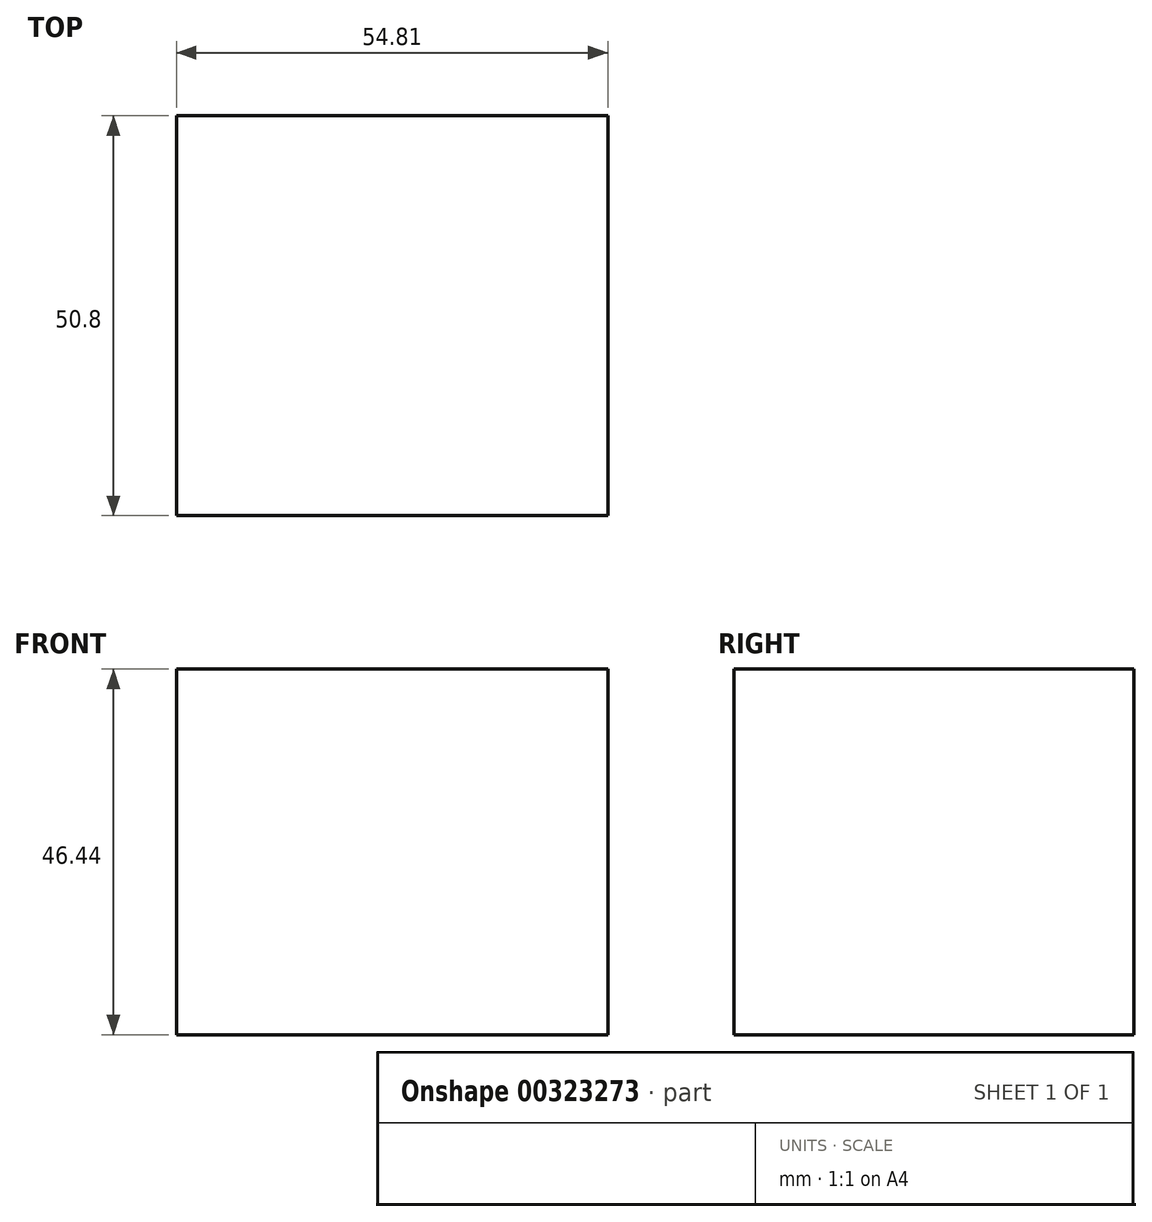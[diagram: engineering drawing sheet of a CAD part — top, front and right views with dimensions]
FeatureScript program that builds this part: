
annotation { "Feature Type Name" : "Feature", "Feature Type Description" : "" }
export const myFeature = defineFeature(function(context is Context, id is Id, definition is map)
    precondition{}
    {
        {
            var Q0;
            Q0=qCreatedBy(makeId("Front.planeOp"),FACE);
            var sketch = newSketch(context, id + "F0", { "sketchPlane" : qUnion([Q0])});
            skLineSegment(sketch, "E0.bottom", {"start": v(-26.77, 20.05) * mm, "end": v(28.04, 20.05) * mm});
            skLineSegment(sketch, "E0.top", {"start": v(-26.77, -26.39) * mm, "end": v(28.04, -26.39) * mm});
            skLineSegment(sketch, "E0.left", {"start": v(-26.77, 20.05) * mm, "end": v(-26.77, -26.39) * mm});
            skLineSegment(sketch, "E0.right", {"start": v(28.04, 20.05) * mm, "end": v(28.04, -26.39) * mm});
            skSolve(sketch);
        }
        {
            var Q0;
            Q0 = qSketchRegion(id + "F0", true);
            extrude(context, id + "F1", {"entities" : qUnion([Q0]), "endBound" : BoundingType.SYMMETRIC, "depth" : 50.8 * mm});
        }
    });
